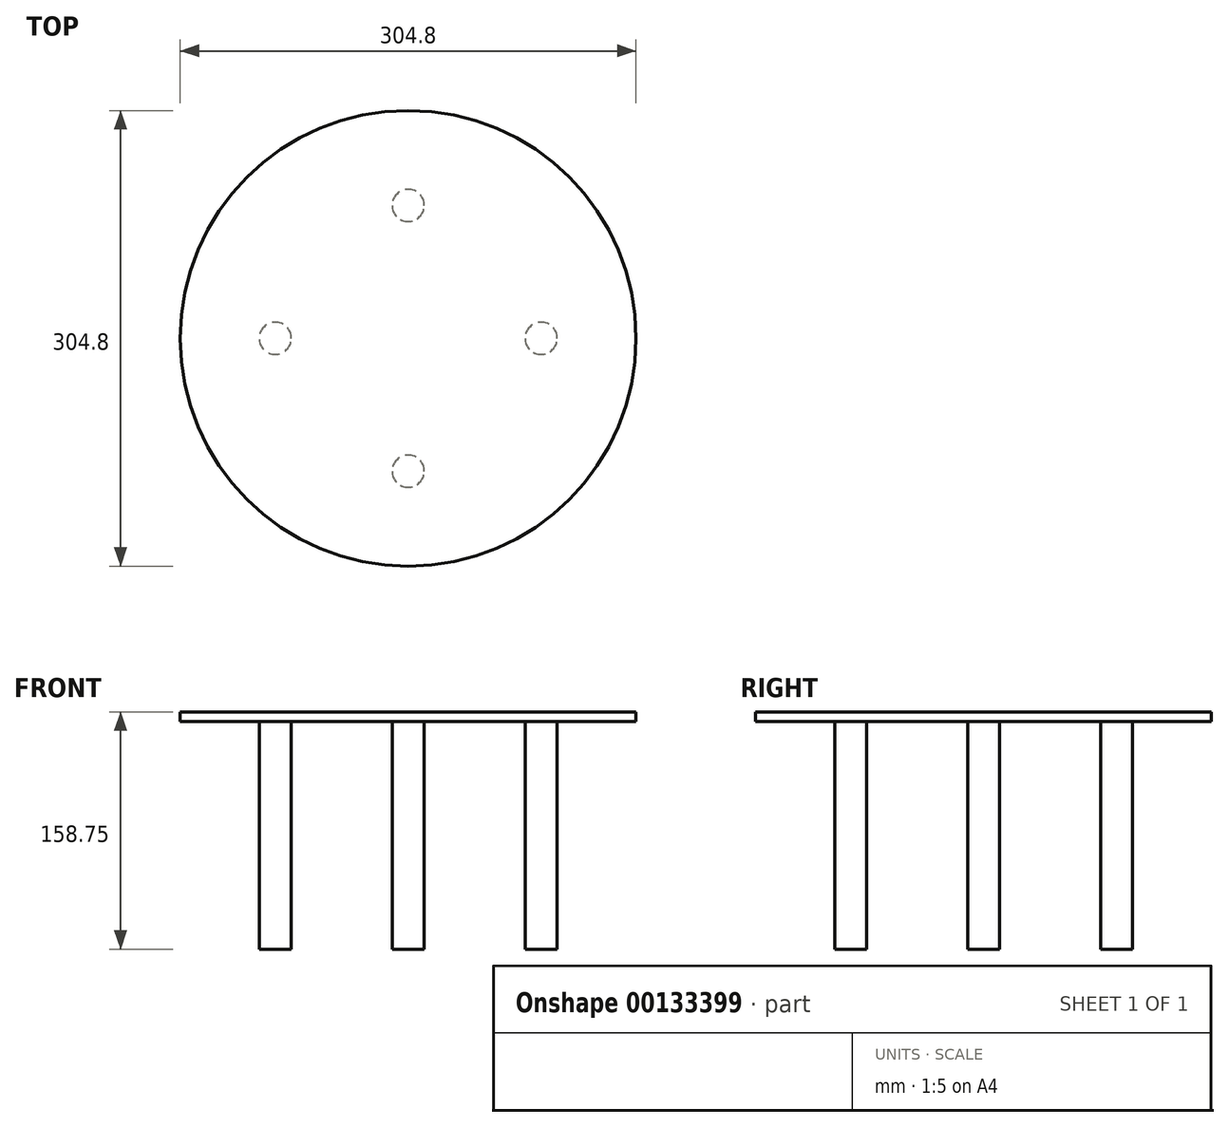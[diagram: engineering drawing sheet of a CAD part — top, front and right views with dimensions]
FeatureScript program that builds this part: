
annotation { "Feature Type Name" : "Feature", "Feature Type Description" : "" }
export const myFeature = defineFeature(function(context is Context, id is Id, definition is map)
    precondition{}
    {
        {
            var Q0;
            Q0=qCreatedBy(makeId("Top.planeOp"),FACE);
            var sketch = newSketch(context, id + "F0", { "sketchPlane" : qUnion([Q0])});
            skCircle(sketch, "E0", {"center": v(0, 0) * mm, "radius": 152.4 * mm});
            skSolve(sketch);
        }
        {
            var Q0;
            Q0 = qSketchRegion(id + "F0", true);
            extrude(context, id + "F1", {"entities" : qUnion([Q0]), "depth" : 6.35 * mm});
        }
        {
            var Q0;
            Q0=makeQuery(id+"F1.opExtrude","CAP_FACE",FACE,{"disambiguationData":[OSD([sQuery(id+"F0.wireOp",EDGE,"E0")])],"isStart":true});
            var sketch = newSketch(context, id + "F2", { "sketchPlane" : qUnion([Q0])});
            skCircle(sketch, "E1", {"center": v(0, 0) * mm, "radius": 88.9 * mm});
            skPoint(sketch, "E2", {"position": v(-88.9, 0) * mm});
            skPoint(sketch, "E3", {"position": v(0, -88.9) * mm});
            skPoint(sketch, "E4", {"position": v(88.9, 0) * mm});
            skPoint(sketch, "E5", {"position": v(0, 88.9) * mm});
            skSolve(sketch);
        }
        {
            var Q0;
            Q0=makeQuery(id+"F2.imprint","IMPRINT",FACE,{"disambiguationData":[TD([[makeQuery(id+"F2.imprint","IMPRINT",EDGE,{"derivedFrom":sQuery(id+"F2.wireOp",EDGE,"E1")}),-1.0]])]});
            var sketch = newSketch(context, id + "F3", { "sketchPlane" : qUnion([Q0])});
            skCircle(sketch, "E6", {"center": v(-88.9, 0) * mm, "radius": 10.72 * mm});
            skCircle(sketch, "E7", {"center": v(0, 88.9) * mm, "radius": 10.72 * mm});
            skCircle(sketch, "E8", {"center": v(0, -88.9) * mm, "radius": 10.72 * mm});
            skCircle(sketch, "E9", {"center": v(88.9, 0) * mm, "radius": 10.72 * mm});
            skSolve(sketch);
        }
        {
            var Q0;
            Q0 = qSketchRegion(id + "F3", true);
            extrude(context, id + "F4", {"entities" : qUnion([Q0]), "operationType" : NewBodyOperationType.ADD, "depth" : 152.4 * mm});
        }
    });
